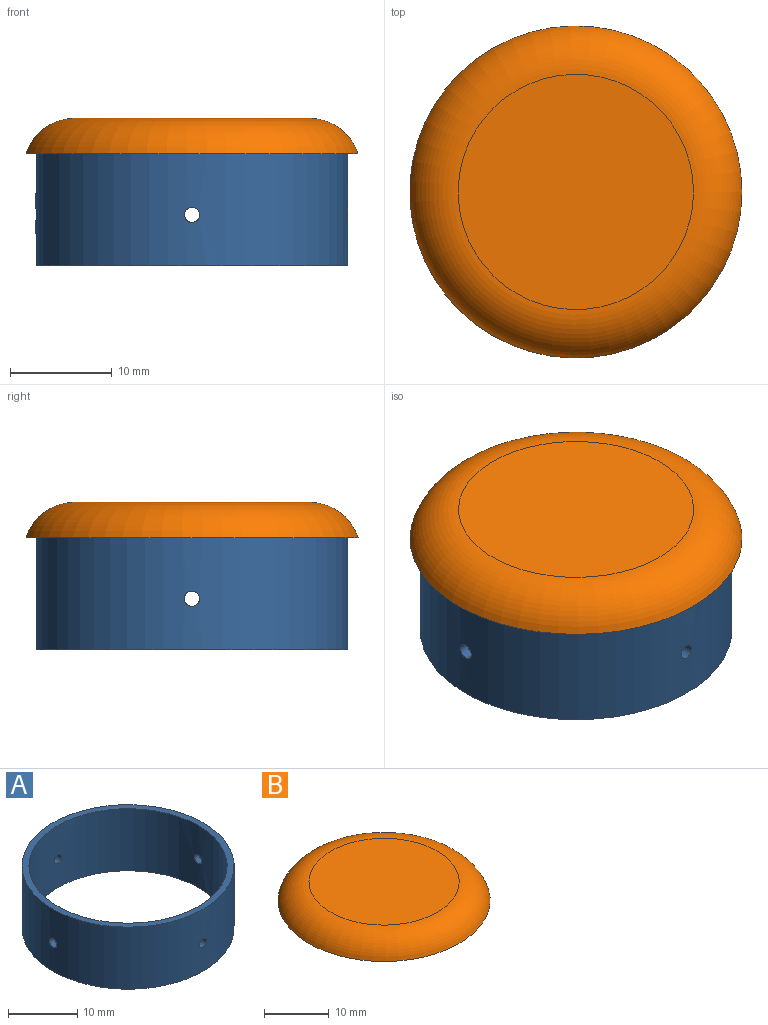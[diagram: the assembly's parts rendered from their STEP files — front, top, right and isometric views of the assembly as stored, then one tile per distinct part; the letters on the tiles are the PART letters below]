
ASSEMBLY  parts=2 mates=1
PART A: 8 faces, bbox 30.7x30.7x11 mm
  f0: cylinder r=14.35mm len=28.7mm, axis (0,0,-1), area 984.7mm2, adj f2,f3,f4,f5,f6,f7
  f1: cylinder r=15.35mm len=30.7mm, axis (0,0,-1), area 1053.9mm2, adj f2,f3,f4,f5,f6,f7
  f2: plane 30.7x30.7mm, normal (0,0,1), area 93.3mm2, adj f0,f1
  f3: plane 30.7x30.7mm, normal (0,0,-1), area 93.3mm2, adj f0,f1
  f4: cylinder r=0.75mm len=1.5mm, axis (1,0,0), area 4.7mm2, adj f0,f1
  f5: cylinder r=0.75mm len=1.5mm, axis (1,0,0), area 4.7mm2, adj f0,f1
  f6: cylinder r=0.75mm len=1.5mm, axis (0,-1,0), area 4.7mm2, adj f0,f1
  f7: cylinder r=0.75mm len=1.5mm, axis (0,-1,0), area 4.7mm2, adj f0,f1
PART B: 5 faces, bbox 35.9x35.9x5 mm
  f0: plane 32.7x32.7mm, normal (0,0,-1), area 177.5mm2, adj f2,f4
  f1: plane 23.16x23.16mm, normal (0,0,1), area 421.3mm2, adj f2
  f2: torus R=11.58mm, axis (0,0,-1), area 570.6mm2, adj f0,f1
  f3: plane 23.16x23.16mm, normal (0,0,-1), area 421.3mm2, adj f4
  f4: torus R=11.58mm, axis (0,0,-1), area 301.2mm2, adj f0,f3
PLACE A t=(1,1.62,2.82)mm
PLACE B t=(1,1.62,17.32)mm
MATE fastened B.f2 <-> A.f1  axis (0,0,-1) through (1,1.62,13.82)mm
